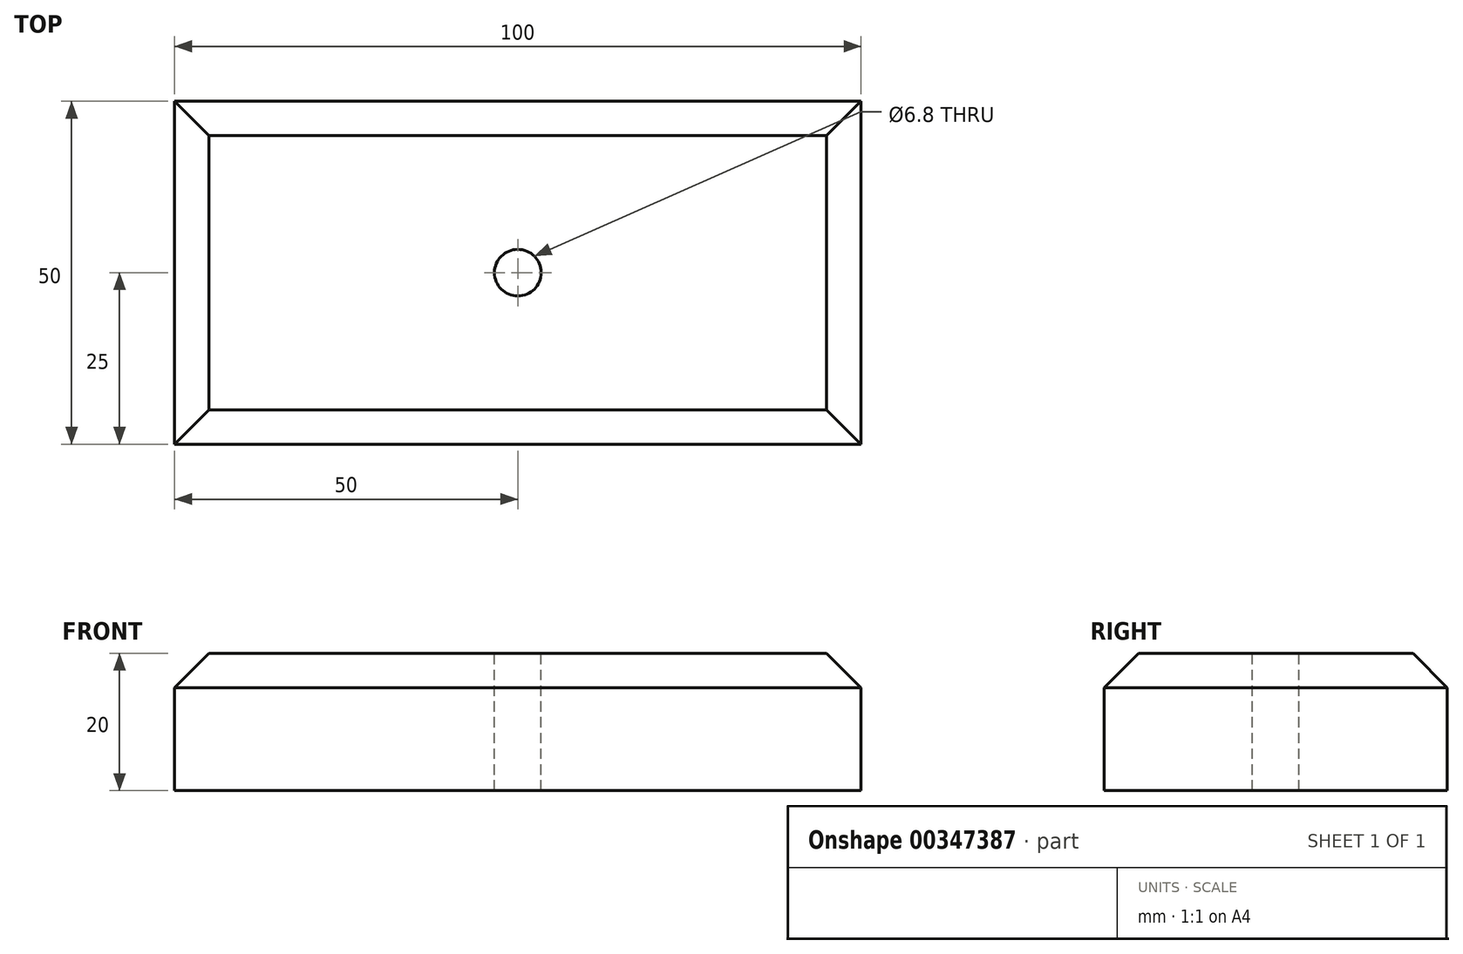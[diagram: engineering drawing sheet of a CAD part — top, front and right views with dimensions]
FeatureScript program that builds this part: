
annotation { "Feature Type Name" : "Feature", "Feature Type Description" : "" }
export const myFeature = defineFeature(function(context is Context, id is Id, definition is map)
    precondition{}
    {
        {
            var Q0;
            Q0=qCreatedBy(makeId("Top.planeOp"),FACE);
            var sketch = newSketch(context, id + "F0", { "sketchPlane" : qUnion([Q0])});
            skLineSegment(sketch, "E0.bottom", {"start": v(-50, 25) * mm, "end": v(50, 25) * mm});
            skLineSegment(sketch, "E0.top", {"start": v(-50, -25) * mm, "end": v(50, -25) * mm});
            skLineSegment(sketch, "E0.left", {"start": v(-50, 25) * mm, "end": v(-50, -25) * mm});
            skLineSegment(sketch, "E0.right", {"start": v(50, 25) * mm, "end": v(50, -25) * mm});
            skPoint(sketch, "E0.middle", {"position": v(0, 0) * mm});
            skSolve(sketch);
        }
        {
            var Q0;
            Q0 = qSketchRegion(id + "F0", true);
            extrude(context, id + "F1", {"entities" : qUnion([Q0]), "endBound" : BoundingType.SYMMETRIC, "depth" : 20 * mm});
        }
        {
            var Q0;
            Q0=makeQuery(id+"F1.opExtrude","CAP_FACE",FACE,{"disambiguationData":[OSD([sQuery(id+"F0.wireOp",EDGE,"E0.bottom"),sQuery(id+"F0.wireOp",EDGE,"E0.top"),sQuery(id+"F0.wireOp",EDGE,"E0.left"),sQuery(id+"F0.wireOp",EDGE,"E0.right")])],"isStart":false});
            var sketch = newSketch(context, id + "F2", { "sketchPlane" : qUnion([Q0])});
            skPoint(sketch, "E1", {"position": v(0, 0) * mm});
            skSolve(sketch);
        }
        {
            var Q0;
            Q0=sQuery(id+"F2.wireOp",VERTEX,"E1");
            var Q1;
            Q1=makeQuery(id+"F1.opExtrude","SWEPT_BODY",BODY,{"disambiguationData":[OSD([sQuery(id+"F0.wireOp",EDGE,"E0.bottom"),sQuery(id+"F0.wireOp",EDGE,"E0.top"),sQuery(id+"F0.wireOp",EDGE,"E0.left"),sQuery(id+"F0.wireOp",EDGE,"E0.right")])]});
            hole(context, id + "F3", {"style" : HoleStyle.SIMPLE, "endStyle" : HoleEndStyle.THROUGH, "standardTappedOrClearance" : lookupTablePath({ "standard" : "ISO", "engagement" : "75%", "pitch" : "1.25 mm", "size" : "M8", "type" : "Gewinde" }), "standardBlindInLast" : lookupTablePath({ "standard" : "ISO", "engagement" : "75%", "pitch" : "1.25 mm", "size" : "M8", "type" : "Gewinde" }), "holeDiameter" : 6.8 * mm, "showTappedDepth" : true, "tappedDepth" : 12 * mm, "tapClearance" : 3, "locations" : qUnion([Q0]), "scope" : qUnion([Q1])});
        }
        {
            var Q0;
            Q0=makeQuery(id+"F1.opExtrude","CAP_EDGE",EDGE,{"disambiguationData":[OSD([sQuery(id+"F0.wireOp",EDGE,"E0.left")])],"isStart":false});
            var Q1;
            Q1=makeQuery(id+"F1.opExtrude","CAP_EDGE",EDGE,{"disambiguationData":[OSD([sQuery(id+"F0.wireOp",EDGE,"E0.top")])],"isStart":false});
            var Q2;
            Q2=makeQuery(id+"F1.opExtrude","CAP_EDGE",EDGE,{"disambiguationData":[OSD([sQuery(id+"F0.wireOp",EDGE,"E0.right")])],"isStart":false});
            var Q3;
            Q3=makeQuery(id+"F1.opExtrude","CAP_EDGE",EDGE,{"disambiguationData":[OSD([sQuery(id+"F0.wireOp",EDGE,"E0.bottom")])],"isStart":false});
            chamfer(context, id + "F4", {"entities" : qUnion([Q0, Q1, Q2, Q3]), "width" : 5 * mm, "tangentPropagation" : true});
        }
    });
